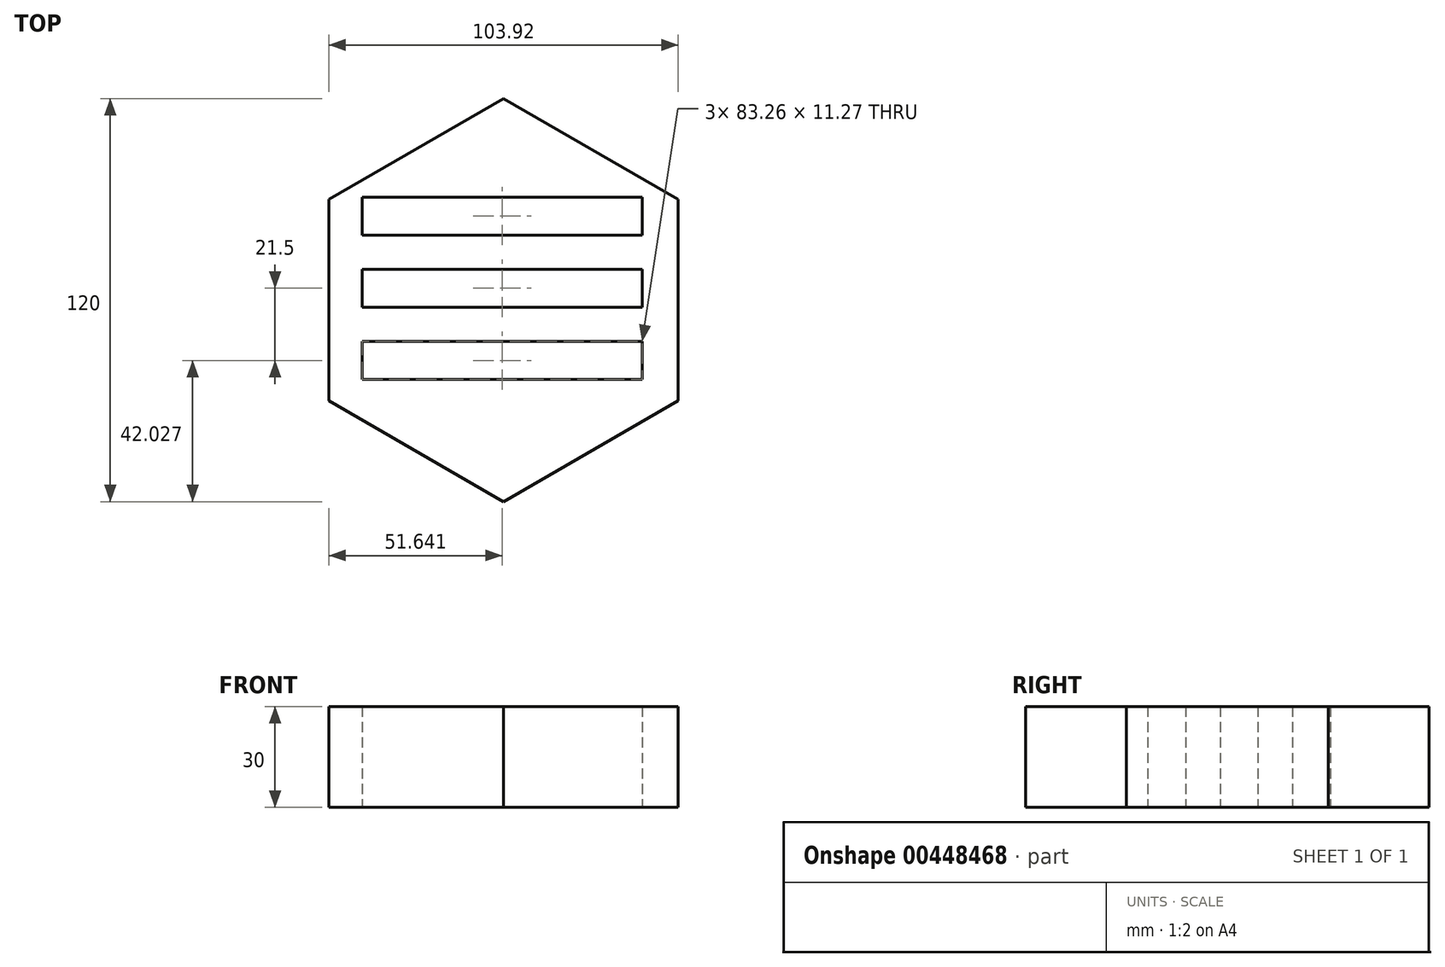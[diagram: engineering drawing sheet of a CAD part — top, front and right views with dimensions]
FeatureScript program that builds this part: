
annotation { "Feature Type Name" : "Feature", "Feature Type Description" : "" }
export const myFeature = defineFeature(function(context is Context, id is Id, definition is map)
    precondition{}
    {
        {
            var Q0;
            Q0=qCreatedBy(makeId("Top.planeOp"),FACE);
            var sketch = newSketch(context, id + "F0", { "sketchPlane" : qUnion([Q0])});
            skCircle(sketch, "E0.cCircle", {"center": v(0, 0) * mm, "radius": 51.96 * mm, "construction": true});
            skLineSegment(sketch, "E0.0", {"start": v(51.96, 30) * mm, "end": v(51.96, -30) * mm});
            skLineSegment(sketch, "E0.1", {"start": v(51.96, -30) * mm, "end": v(0, -60) * mm});
            skLineSegment(sketch, "E0.2", {"start": v(0, -60) * mm, "end": v(-51.96, -30) * mm});
            skLineSegment(sketch, "E0.3", {"start": v(-51.96, -30) * mm, "end": v(-51.96, 30) * mm});
            skLineSegment(sketch, "E0.4", {"start": v(-51.96, 30) * mm, "end": v(0, 60) * mm});
            skLineSegment(sketch, "E0.5", {"start": v(0, 60) * mm, "end": v(51.96, 30) * mm});
            skPoint(sketch, "E0.0.midPoint", {"position": v(51.96, 0) * mm});
            skLineSegment(sketch, "E1.bottom", {"start": v(-41.95, 30.66) * mm, "end": v(41.31, 30.66) * mm});
            skLineSegment(sketch, "E1.top", {"start": v(-41.95, 19.4) * mm, "end": v(41.31, 19.4) * mm});
            skLineSegment(sketch, "E1.left", {"start": v(-41.95, 30.66) * mm, "end": v(-41.95, 19.4) * mm});
            skLineSegment(sketch, "E1.right", {"start": v(41.31, 30.66) * mm, "end": v(41.31, 19.4) * mm});
            skLineSegment(sketch, "E2.0.1.0", {"start": v(-41.95, 9.16) * mm, "end": v(41.31, 9.16) * mm});
            skLineSegment(sketch, "E2.0.1.1", {"start": v(-41.95, 9.16) * mm, "end": v(-41.95, -2.1) * mm});
            skLineSegment(sketch, "E2.0.1.2", {"start": v(-41.95, -2.1) * mm, "end": v(41.31, -2.1) * mm});
            skLineSegment(sketch, "E2.0.1.3", {"start": v(41.31, 9.16) * mm, "end": v(41.31, -2.1) * mm});
            skLineSegment(sketch, "E2.0.2.0", {"start": v(-41.95, -12.34) * mm, "end": v(41.31, -12.34) * mm});
            skLineSegment(sketch, "E2.0.2.1", {"start": v(-41.95, -12.34) * mm, "end": v(-41.95, -23.6) * mm});
            skLineSegment(sketch, "E2.0.2.2", {"start": v(-41.95, -23.6) * mm, "end": v(41.31, -23.6) * mm});
            skLineSegment(sketch, "E2.0.2.3", {"start": v(41.31, -12.34) * mm, "end": v(41.31, -23.6) * mm});
            skLineSegment(sketch, "E2.direction1", {"start": v(-41.95, 19.4) * mm, "end": v(-16.95, 19.4) * mm, "construction": true});
            skLineSegment(sketch, "E2.direction2", {"start": v(-41.95, 19.4) * mm, "end": v(-41.95, -2.1) * mm, "construction": true});
            skSolve(sketch);
        }
        {
            var Q0;
            Q0=makeQuery(id+"F0.imprint","IMPRINT",FACE,{"disambiguationData":[TD([[makeQuery(id+"F0.imprint","IMPRINT",EDGE,{"derivedFrom":sQuery(id+"F0.wireOp",EDGE,"E0.0")}),-1.0]])]});
            extrude(context, id + "F1", {"entities" : qUnion([Q0]), "depth" : 30 * mm});
        }
    });
